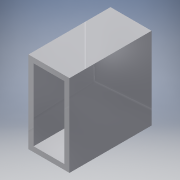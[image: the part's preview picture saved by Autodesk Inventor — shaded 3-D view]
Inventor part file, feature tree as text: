
AUTODESK INVENTOR PART (.ipt)
format: ipt  version: 2016 (Build 200138000, 138)  size: 100,352 bytes
history: native  units: in
note: dims shown in document units (in); Inventor stores cm internally (conversion verified against a paired STEP export)
features: extrude x1, sketch x1
ambient origin geometry x8: Origin, YZ Plane, XZ Plane, XY Plane, X Axis, Y Axis, Z Axis, Center Point
bodies: Solid1 (feature_tree)
feature tree (2):
  extrude  "Extrusion1"  Depth=2.0in
  sketch  "Sketch1"  dims[d0=1.0in d1=2.0in d2=0.125in d3=0.125in d4=0.125in d5=0.125in d6=2.0in d7=0.0in]
